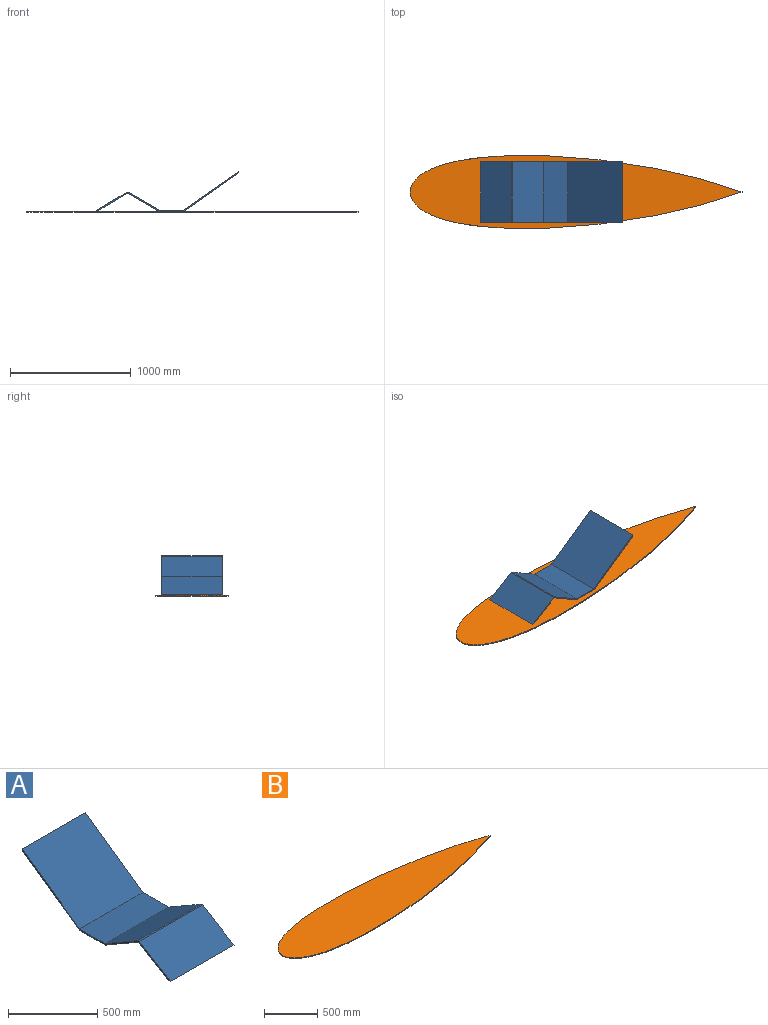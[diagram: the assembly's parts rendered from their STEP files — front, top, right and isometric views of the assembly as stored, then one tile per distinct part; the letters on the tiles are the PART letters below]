
ASSEMBLY  parts=2 mates=1
PART A: 15 faces, bbox 500x1176.6x329 mm
  f0: plane 500x457.01mm, normal (0,-0.57,0.82), area 278951.5mm2, adj f1,f12,f13,f14
  f1: plane 500x200mm, normal (0,0,1), area 100000mm2, adj f0,f2,f13,f14
  f2: plane 500x259.81mm, normal (0,0.5,0.87), area 150000mm2, adj f1,f3,f13,f14
  f3: plane 500x9.12mm, normal (0,-0.01,1), area 4559.9mm2, adj f2,f4,f13,f14
  f4: plane 500x250.69mm, normal (0,-0.51,0.86), area 146050.9mm2, adj f3,f5,f13,f14
  f5: plane 500x17.53mm, normal (0,0,-1), area 8767.2mm2, adj f4,f6,f13,f14
  f6: plane 500x237.77mm, normal (0,0.51,-0.86), area 138526.7mm2, adj f5,f7,f13,f14
  f7: plane 500x259.81mm, normal (0,-0.5,-0.87), area 150000mm2, adj f6,f8,f13,f14
  f8: plane 500x4.5mm, normal (0,-0.26,-0.97), area 2329.4mm2, adj f7,f9,f13,f14
  f9: plane 500x200mm, normal (0,0,-1), area 100000mm2, adj f8,f10,f13,f14
  f10: plane 500x5.16mm, normal (0,0.3,-0.95), area 2706.4mm2, adj f9,f11,f13,f14
  f11: plane 500x451.85mm, normal (0,0.57,-0.82), area 275800.6mm2, adj f10,f12,f13,f14
  f12: plane 500x10.99mm, normal (0,1,0), area 5493.5mm2, adj f0,f11,f13,f14
  f13: plane 1176.62x329mm, normal (1,0,0), area 12132.8mm2, adj f0,f1,f2,f3,f4,f5,f6,f7
  f14: plane 1176.62x329mm, normal (-1,0,0), area 12132.8mm2, adj f0,f1,f2,f3,f4,f5,f6,f7
PART B: 4 faces, bbox 2750x863.1x9 mm
  f0: extruded ~2750x302.92mm, area 26043.8mm2, adj f1,f2,f3
  f1: extruded ~2750x302.92mm, area 26043.8mm2, adj f0,f2,f3
  f2: plane 2750x863.12mm, normal (0,0,1), area 1198710mm2, adj f0,f1
  f3: plane 2750x863.12mm, normal (0,0,-1), area 1198710mm2, adj f0,f1
PLACE A rot(axis=(0,0,-1),90deg) t=(273.03,72.83,114.7)mm
PLACE B t=(312.72,72.83,-23.88)mm
MATE fastened A.f9 <-> B.f2  axis (0,0,-1) through (419.41,72.83,-14.88)mm
